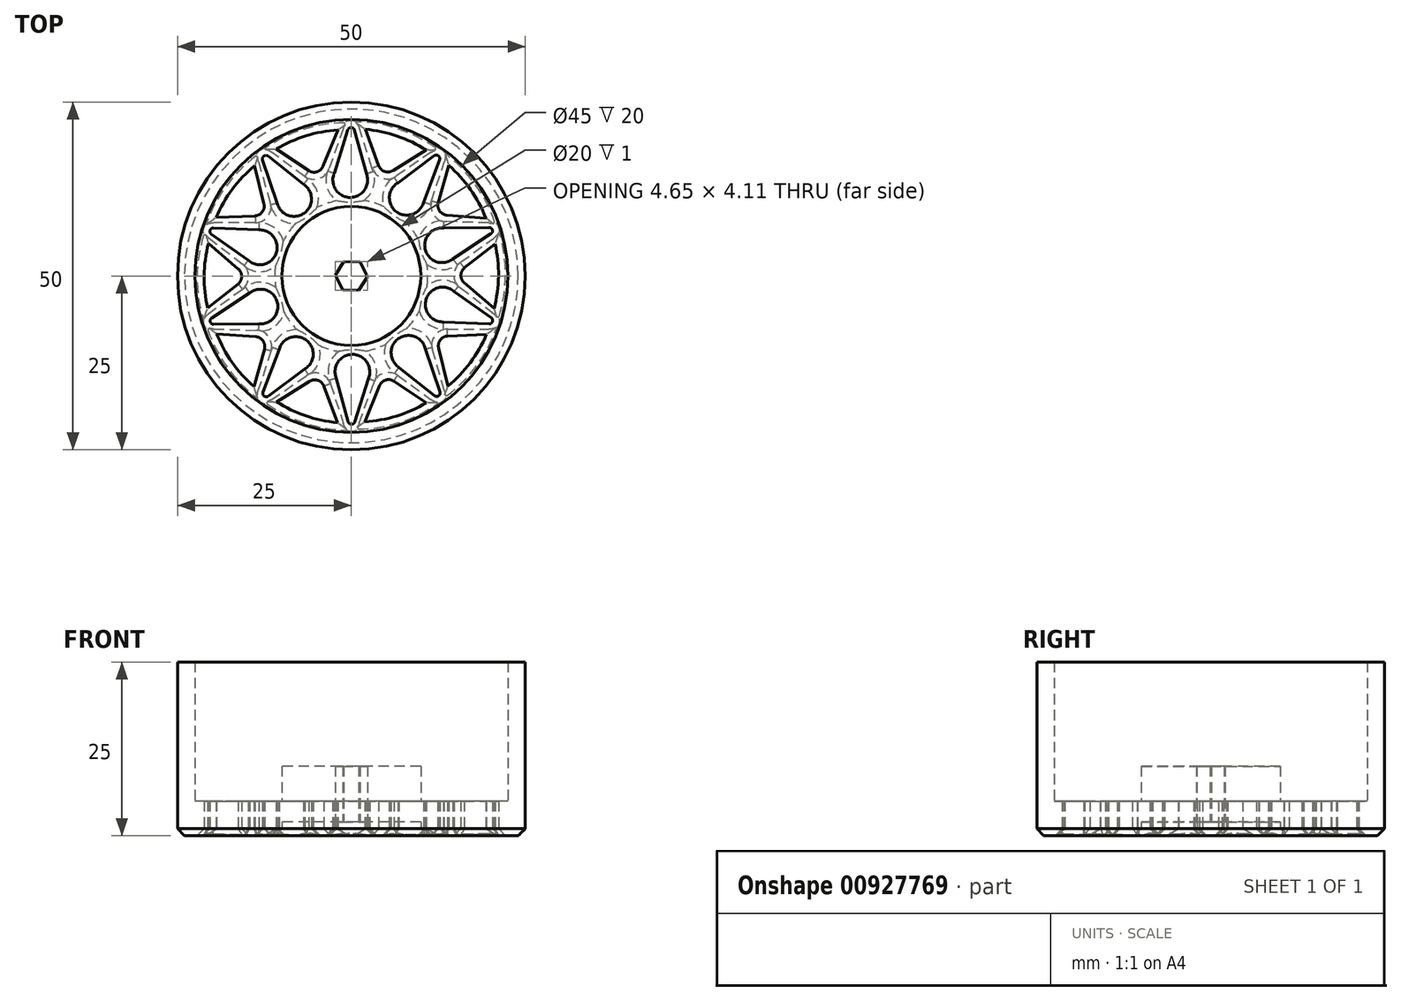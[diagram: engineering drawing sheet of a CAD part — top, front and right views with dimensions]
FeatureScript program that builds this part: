
annotation { "Feature Type Name" : "Feature", "Feature Type Description" : "" }
export const myFeature = defineFeature(function(context is Context, id is Id, definition is map)
    precondition{}
    {
        {
            var Q0;
            Q0=qCreatedBy(makeId("Top.planeOp"),FACE);
            var sketch = newSketch(context, id + "F0", { "sketchPlane" : qUnion([Q0])});
            skCircle(sketch, "E0", {"center": v(0, 0) * mm, "radius": 25 * mm});
            skCircle(sketch, "E1", {"center": v(0, 0) * mm, "radius": 22.5 * mm});
            skCircle(sketch, "E2", {"center": v(0, 0) * mm, "radius": 10 * mm});
            skLineSegment(sketch, "E3", {"start": v(0, 10) * mm, "end": v(0, 22.5) * mm, "construction": true});
            skPoint(sketch, "E4", {"position": v(0, 16.25) * mm});
            skCircle(sketch, "E5", {"center": v(-0.16, 13.78) * mm, "radius": 2.5 * mm});
            skPoint(sketch, "E6", {"position": v(0, 22.61) * mm});
            skLineSegment(sketch, "E7", {"start": v(-2.63, 14.21) * mm, "end": v(2.3, 14.21) * mm, "construction": true});
            skLineSegment(sketch, "E8", {"start": v(-0.5, 20.99) * mm, "end": v(-2.63, 14.21) * mm});
            skLineSegment(sketch, "E9", {"start": v(0.45, 20.97) * mm, "end": v(2.3, 14.21) * mm});
            skArc(sketch, "E10.filletArc", {"start": v(0.45, 20.97) * mm, "mid": v(-0.02, 21.34) * mm, "end": v(-0.5, 20.99) * mm});
            skCircle(sketch, "E11.1.0", {"center": v(-8.23, 11.06) * mm, "radius": 2.5 * mm});
            skLineSegment(sketch, "E11.1.1", {"start": v(-11.96, 17.23) * mm, "end": v(-6.49, 12.85) * mm});
            skLineSegment(sketch, "E11.1.2", {"start": v(-12.75, 16.68) * mm, "end": v(-10.48, 9.95) * mm});
            skArc(sketch, "E11.1.3", {"start": v(-11.96, 17.23) * mm, "mid": v(-12.56, 17.25) * mm, "end": v(-12.75, 16.68) * mm});
            skCircle(sketch, "E11.2.0", {"center": v(-13.15, 4.11) * mm, "radius": 2.5 * mm});
            skLineSegment(sketch, "E11.2.1", {"start": v(-19.8, 6.9) * mm, "end": v(-12.8, 6.59) * mm});
            skLineSegment(sketch, "E11.2.2", {"start": v(-20.12, 6) * mm, "end": v(-14.33, 1.9) * mm});
            skArc(sketch, "E11.2.3", {"start": v(-19.8, 6.9) * mm, "mid": v(-20.3, 6.57) * mm, "end": v(-20.12, 6) * mm});
            skCircle(sketch, "E11.3.0", {"center": v(-13.06, -4.4) * mm, "radius": 2.5 * mm});
            skLineSegment(sketch, "E11.3.1", {"start": v(-20.08, -6.05) * mm, "end": v(-14.23, -2.2) * mm});
            skLineSegment(sketch, "E11.3.2", {"start": v(-19.8, -6.97) * mm, "end": v(-12.7, -6.89) * mm});
            skArc(sketch, "E11.3.3", {"start": v(-20.08, -6.05) * mm, "mid": v(-20.29, -6.61) * mm, "end": v(-19.8, -6.97) * mm});
            skCircle(sketch, "E11.4.0", {"center": v(-7.97, -11.24) * mm, "radius": 2.5 * mm});
            skLineSegment(sketch, "E11.4.1", {"start": v(-12.7, -16.7) * mm, "end": v(-10.22, -10.14) * mm});
            skLineSegment(sketch, "E11.4.2", {"start": v(-11.92, -17.28) * mm, "end": v(-6.23, -13.04) * mm});
            skArc(sketch, "E11.4.3", {"start": v(-12.7, -16.7) * mm, "mid": v(-12.52, -17.28) * mm, "end": v(-11.92, -17.28) * mm});
            skCircle(sketch, "E11.5.0", {"center": v(0.16, -13.78) * mm, "radius": 2.5 * mm});
            skLineSegment(sketch, "E11.5.1", {"start": v(-0.45, -20.97) * mm, "end": v(-2.3, -14.21) * mm});
            skLineSegment(sketch, "E11.5.2", {"start": v(0.5, -20.99) * mm, "end": v(2.63, -14.21) * mm});
            skArc(sketch, "E11.5.3", {"start": v(-0.45, -20.97) * mm, "mid": v(0.02, -21.34) * mm, "end": v(0.5, -20.99) * mm});
            skCircle(sketch, "E11.6.0", {"center": v(8.23, -11.06) * mm, "radius": 2.5 * mm});
            skLineSegment(sketch, "E11.6.1", {"start": v(11.96, -17.23) * mm, "end": v(6.49, -12.85) * mm});
            skLineSegment(sketch, "E11.6.2", {"start": v(12.75, -16.68) * mm, "end": v(10.48, -9.95) * mm});
            skArc(sketch, "E11.6.3", {"start": v(11.96, -17.23) * mm, "mid": v(12.56, -17.25) * mm, "end": v(12.75, -16.68) * mm});
            skCircle(sketch, "E11.7.0", {"center": v(13.15, -4.11) * mm, "radius": 2.5 * mm});
            skLineSegment(sketch, "E11.7.1", {"start": v(19.8, -6.9) * mm, "end": v(12.8, -6.59) * mm});
            skLineSegment(sketch, "E11.7.2", {"start": v(20.12, -6) * mm, "end": v(14.33, -1.9) * mm});
            skArc(sketch, "E11.7.3", {"start": v(19.8, -6.9) * mm, "mid": v(20.3, -6.57) * mm, "end": v(20.12, -6) * mm});
            skCircle(sketch, "E11.8.0", {"center": v(13.06, 4.4) * mm, "radius": 2.5 * mm});
            skLineSegment(sketch, "E11.8.1", {"start": v(20.08, 6.05) * mm, "end": v(14.23, 2.2) * mm});
            skLineSegment(sketch, "E11.8.2", {"start": v(19.8, 6.97) * mm, "end": v(12.7, 6.89) * mm});
            skArc(sketch, "E11.8.3", {"start": v(20.08, 6.05) * mm, "mid": v(20.29, 6.61) * mm, "end": v(19.8, 6.97) * mm});
            skCircle(sketch, "E11.9.0", {"center": v(7.97, 11.24) * mm, "radius": 2.5 * mm});
            skLineSegment(sketch, "E11.9.1", {"start": v(12.7, 16.7) * mm, "end": v(10.22, 10.14) * mm});
            skLineSegment(sketch, "E11.9.2", {"start": v(11.92, 17.28) * mm, "end": v(6.23, 13.04) * mm});
            skArc(sketch, "E11.9.3", {"start": v(12.7, 16.7) * mm, "mid": v(12.52, 17.28) * mm, "end": v(11.92, 17.28) * mm});
            skLineSegment(sketch, "E12", {"start": v(-10.78, 18.23) * mm, "end": v(-6.12, 15.12) * mm});
            skPoint(sketch, "E12.endSnap0", {"position": v(-9.22, 15.04) * mm});
            skLineSegment(sketch, "E13", {"start": v(-1.93, 20.97) * mm, "end": v(-4.06, 15.78) * mm});
            skArc(sketch, "E14", {"start": v(-6.12, 15.12) * mm, "mid": v(-4.94, 14.97) * mm, "end": v(-4.06, 15.78) * mm});
            skArc(sketch, "E15", {"start": v(-1.93, 20.97) * mm, "mid": v(-6.52, 20.14) * mm, "end": v(-10.78, 18.23) * mm});
            skLineSegment(sketch, "E16.1.0", {"start": v(-19.44, 8.41) * mm, "end": v(-13.84, 8.64) * mm});
            skArc(sketch, "E16.1.1", {"start": v(-13.84, 8.64) * mm, "mid": v(-12.8, 9.21) * mm, "end": v(-12.56, 10.38) * mm});
            skLineSegment(sketch, "E16.1.2", {"start": v(-13.9, 15.83) * mm, "end": v(-12.56, 10.38) * mm});
            skArc(sketch, "E16.1.3", {"start": v(-13.9, 15.83) * mm, "mid": v(-17.11, 12.46) * mm, "end": v(-19.44, 8.41) * mm});
            skLineSegment(sketch, "E16.2.0", {"start": v(-20.67, -4.62) * mm, "end": v(-16.27, -1.15) * mm});
            skArc(sketch, "E16.2.1", {"start": v(-16.27, -1.15) * mm, "mid": v(-15.76, -0.07) * mm, "end": v(-16.26, 1.01) * mm});
            skLineSegment(sketch, "E16.2.2", {"start": v(-20.54, 4.65) * mm, "end": v(-16.26, 1.01) * mm});
            skArc(sketch, "E16.2.3", {"start": v(-20.54, 4.65) * mm, "mid": v(-21.17, 0.02) * mm, "end": v(-20.67, -4.62) * mm});
            skLineSegment(sketch, "E16.3.0", {"start": v(-14, -15.89) * mm, "end": v(-12.5, -10.5) * mm});
            skArc(sketch, "E16.3.1", {"start": v(-12.5, -10.5) * mm, "mid": v(-12.71, -9.32) * mm, "end": v(-13.75, -8.74) * mm});
            skLineSegment(sketch, "E16.3.2", {"start": v(-19.35, -8.32) * mm, "end": v(-13.75, -8.74) * mm});
            skArc(sketch, "E16.3.3", {"start": v(-19.35, -8.32) * mm, "mid": v(-17.14, -12.42) * mm, "end": v(-14, -15.89) * mm});
            skLineSegment(sketch, "E16.4.0", {"start": v(-2, -21.09) * mm, "end": v(-3.94, -15.83) * mm});
            skArc(sketch, "E16.4.1", {"start": v(-3.94, -15.83) * mm, "mid": v(-4.8, -15.01) * mm, "end": v(-5.99, -15.15) * mm});
            skLineSegment(sketch, "E16.4.2", {"start": v(-10.77, -18.1) * mm, "end": v(-5.99, -15.15) * mm});
            skArc(sketch, "E16.4.3", {"start": v(-10.77, -18.1) * mm, "mid": v(-6.56, -20.12) * mm, "end": v(-2, -21.09) * mm});
            skLineSegment(sketch, "E16.5.0", {"start": v(10.78, -18.23) * mm, "end": v(6.12, -15.12) * mm});
            skArc(sketch, "E16.5.1", {"start": v(6.12, -15.12) * mm, "mid": v(4.94, -14.97) * mm, "end": v(4.06, -15.78) * mm});
            skLineSegment(sketch, "E16.5.2", {"start": v(1.93, -20.97) * mm, "end": v(4.06, -15.78) * mm});
            skArc(sketch, "E16.5.3", {"start": v(1.93, -20.97) * mm, "mid": v(6.52, -20.14) * mm, "end": v(10.78, -18.23) * mm});
            skLineSegment(sketch, "E16.6.0", {"start": v(19.44, -8.41) * mm, "end": v(13.84, -8.64) * mm});
            skArc(sketch, "E16.6.1", {"start": v(13.84, -8.64) * mm, "mid": v(12.8, -9.21) * mm, "end": v(12.56, -10.38) * mm});
            skLineSegment(sketch, "E16.6.2", {"start": v(13.9, -15.83) * mm, "end": v(12.56, -10.38) * mm});
            skArc(sketch, "E16.6.3", {"start": v(13.9, -15.83) * mm, "mid": v(17.11, -12.46) * mm, "end": v(19.44, -8.41) * mm});
            skLineSegment(sketch, "E16.7.0", {"start": v(20.67, 4.62) * mm, "end": v(16.27, 1.15) * mm});
            skArc(sketch, "E16.7.1", {"start": v(16.27, 1.15) * mm, "mid": v(15.76, 0.07) * mm, "end": v(16.26, -1.01) * mm});
            skLineSegment(sketch, "E16.7.2", {"start": v(20.54, -4.65) * mm, "end": v(16.26, -1.01) * mm});
            skArc(sketch, "E16.7.3", {"start": v(20.54, -4.65) * mm, "mid": v(21.17, -0.02) * mm, "end": v(20.67, 4.62) * mm});
            skLineSegment(sketch, "E16.8.0", {"start": v(14, 15.89) * mm, "end": v(12.5, 10.5) * mm});
            skArc(sketch, "E16.8.1", {"start": v(12.5, 10.5) * mm, "mid": v(12.71, 9.32) * mm, "end": v(13.75, 8.74) * mm});
            skLineSegment(sketch, "E16.8.2", {"start": v(19.35, 8.32) * mm, "end": v(13.75, 8.74) * mm});
            skArc(sketch, "E16.8.3", {"start": v(19.35, 8.32) * mm, "mid": v(17.14, 12.42) * mm, "end": v(14, 15.89) * mm});
            skLineSegment(sketch, "E16.9.0", {"start": v(2, 21.09) * mm, "end": v(3.94, 15.83) * mm});
            skArc(sketch, "E16.9.1", {"start": v(3.94, 15.83) * mm, "mid": v(4.8, 15.01) * mm, "end": v(5.99, 15.15) * mm});
            skLineSegment(sketch, "E16.9.2", {"start": v(10.77, 18.1) * mm, "end": v(5.99, 15.15) * mm});
            skArc(sketch, "E16.9.3", {"start": v(10.77, 18.1) * mm, "mid": v(6.56, 20.12) * mm, "end": v(2, 21.09) * mm});
            skSolve(sketch);
        }
        {
            var Q0;
            Q0=makeQuery(id+"F0.imprint","IMPRINT",FACE,{"disambiguationData":[TD([[makeQuery(id+"F0.imprint","IMPRINT",EDGE,{"derivedFrom":sQuery(id+"F0.wireOp",EDGE,"E0")}),1.0]])]});
            extrude(context, id + "F1", {"entities" : qUnion([Q0]), "depth" : 25 * mm, "offsetDistance" : 25 * mm});
        }
        {
            var Q0;
            Q0=makeQuery(id+"F0.imprint","IMPRINT",FACE,{"disambiguationData":[TD([[makeQuery(id+"F0.imprint","IMPRINT",EDGE,{"derivedFrom":sQuery(id+"F0.wireOp",EDGE,"E1")}),1.0]])]});
            extrude(context, id + "F2", {"entities" : qUnion([Q0]), "operationType" : NewBodyOperationType.ADD, "depth" : 5 * mm, "offsetDistance" : 25 * mm});
        }
        {
            var Q0;
            {var subQ0=sQuery(id+"F0.wireOp",EDGE,"E2");var subQ1=makeQuery(id+"F0.imprint","INTERSECT",VERTEX,{"derivedFrom":[subQ0,sQuery(id+"F0.wireOp",EDGE,"FMw9U3Ag-M4uU-eOUw-AIyu-Y3kzjyrUIhWa.right")]});Q0=makeQuery(id+"F0.imprint","IMPRINT",FACE,{"disambiguationData":[TD([[makeQuery(id+"F0.imprint","IMPRINT",EDGE,{"disambiguationData":[TD([[subQ1,1.0]])],"derivedFrom":subQ0}),1.0]])]});}
            extrude(context, id + "F3", {"entities" : qUnion([Q0]), "operationType" : NewBodyOperationType.ADD, "depth" : 10 * mm, "offsetDistance" : 25 * mm});
        }
        {
            var Q0;
            Q0=makeQuery(id+"F0.imprint","IMPRINT",FACE,{"disambiguationData":[TD([[makeQuery(id+"F0.imprint","IMPRINT",EDGE,{"derivedFrom":sQuery(id+"F0.wireOp",EDGE,"E2")}),1.0]])]});
            extrude(context, id + "F4", {"entities" : qUnion([Q0]), "operationType" : NewBodyOperationType.REMOVE, "depth" : 2 * mm, "offsetDistance" : 25 * mm});
        }
        {
            var Q0;
            Q0=makeQuery(id+"F0.imprint","IMPRINT",FACE,{"disambiguationData":[TD([[makeQuery(id+"F0.imprint","IMPRINT",EDGE,{"derivedFrom":sQuery(id+"F0.wireOp",EDGE,"E2")}),1.0]])]});
            var sketch = newSketch(context, id + "F5", { "sketchPlane" : qUnion([Q0])});
            skPoint(sketch, "E17.0.midPoint", {"position": v(-1.32, 0.78) * mm});
            skCircle(sketch, "E18.cCircle", {"center": v(0, 0) * mm, "radius": 2.02 * mm, "construction": true});
            skLineSegment(sketch, "E18.0", {"start": v(-2.33, 0.08) * mm, "end": v(-1.1, 2.06) * mm});
            skLineSegment(sketch, "E18.1", {"start": v(-1.1, 2.06) * mm, "end": v(1.24, 1.97) * mm});
            skLineSegment(sketch, "E18.2", {"start": v(1.24, 1.97) * mm, "end": v(2.33, -0.08) * mm});
            skLineSegment(sketch, "E18.3", {"start": v(2.33, -0.08) * mm, "end": v(1.1, -2.06) * mm});
            skLineSegment(sketch, "E18.4", {"start": v(1.1, -2.06) * mm, "end": v(-1.24, -1.97) * mm});
            skLineSegment(sketch, "E18.5", {"start": v(-1.24, -1.97) * mm, "end": v(-2.33, 0.08) * mm});
            skPoint(sketch, "E18.0.midPoint", {"position": v(-1.7, 1.07) * mm});
            skPoint(sketch, "E19.orphan", {"position": v(-0.9, -1.52) * mm});
            skPoint(sketch, "E20.orphan", {"position": v(0.87, -1.54) * mm});
            skPoint(sketch, "E21.orphan", {"position": v(-1.77, 0.02) * mm});
            skPoint(sketch, "E17.1.start.orphan", {"position": v(-0.87, 1.54) * mm});
            skCircle(sketch, "E22.cCircle", {"center": v(0, -5.83) * mm, "radius": 1.3 * mm, "construction": true});
            skLineSegment(sketch, "E22.0", {"start": v(0.95, -7.14) * mm, "end": v(-0.95, -7.14) * mm});
            skLineSegment(sketch, "E22.1", {"start": v(-0.95, -7.14) * mm, "end": v(-1.54, -5.33) * mm});
            skLineSegment(sketch, "E22.2", {"start": v(-1.54, -5.33) * mm, "end": v(0, -4.21) * mm});
            skLineSegment(sketch, "E22.3", {"start": v(0, -4.21) * mm, "end": v(1.54, -5.33) * mm});
            skLineSegment(sketch, "E22.4", {"start": v(1.54, -5.33) * mm, "end": v(0.95, -7.14) * mm});
            skPoint(sketch, "E22.0.midPoint", {"position": v(0, -7.14) * mm});
            skLineSegment(sketch, "E23.1.0", {"start": v(5.54, -0.18) * mm, "end": v(7.08, -1.3) * mm});
            skLineSegment(sketch, "E23.1.1", {"start": v(4, -1.3) * mm, "end": v(5.54, -0.18) * mm});
            skLineSegment(sketch, "E23.1.2", {"start": v(4.6, -3.11) * mm, "end": v(4, -1.3) * mm});
            skLineSegment(sketch, "E23.1.3", {"start": v(6.5, -3.11) * mm, "end": v(4.6, -3.11) * mm});
            skLineSegment(sketch, "E23.1.4", {"start": v(7.08, -1.3) * mm, "end": v(6.5, -3.11) * mm});
            skLineSegment(sketch, "E23.2.0", {"start": v(1.89, 5.22) * mm, "end": v(3.43, 6.33) * mm});
            skLineSegment(sketch, "E23.2.1", {"start": v(2.47, 3.4) * mm, "end": v(1.89, 5.22) * mm});
            skLineSegment(sketch, "E23.2.2", {"start": v(4.38, 3.4) * mm, "end": v(2.47, 3.4) * mm});
            skLineSegment(sketch, "E23.2.3", {"start": v(4.97, 5.22) * mm, "end": v(4.38, 3.4) * mm});
            skLineSegment(sketch, "E23.2.4", {"start": v(3.43, 6.33) * mm, "end": v(4.97, 5.22) * mm});
            skLineSegment(sketch, "E23.3.0", {"start": v(-4.38, 3.4) * mm, "end": v(-4.97, 5.22) * mm});
            skLineSegment(sketch, "E23.3.1", {"start": v(-2.47, 3.4) * mm, "end": v(-4.38, 3.4) * mm});
            skLineSegment(sketch, "E23.3.2", {"start": v(-1.89, 5.22) * mm, "end": v(-2.47, 3.4) * mm});
            skLineSegment(sketch, "E23.3.3", {"start": v(-3.43, 6.33) * mm, "end": v(-1.89, 5.22) * mm});
            skLineSegment(sketch, "E23.3.4", {"start": v(-4.97, 5.22) * mm, "end": v(-3.43, 6.33) * mm});
            skLineSegment(sketch, "E23.4.0", {"start": v(-4.6, -3.11) * mm, "end": v(-6.5, -3.11) * mm});
            skLineSegment(sketch, "E23.4.1", {"start": v(-4, -1.3) * mm, "end": v(-4.6, -3.11) * mm});
            skLineSegment(sketch, "E23.4.2", {"start": v(-5.54, -0.18) * mm, "end": v(-4, -1.3) * mm});
            skLineSegment(sketch, "E23.4.3", {"start": v(-7.08, -1.3) * mm, "end": v(-5.54, -0.18) * mm});
            skLineSegment(sketch, "E23.4.4", {"start": v(-6.5, -3.11) * mm, "end": v(-7.08, -1.3) * mm});
            skSolve(sketch);
        }
        {
            var Q0;
            Q0=makeQuery(id+"F5.imprint","IMPRINT",FACE,{"disambiguationData":[TD([[makeQuery(id+"F5.imprint","IMPRINT",EDGE,{"derivedFrom":sQuery(id+"F5.wireOp",EDGE,"E18.0")}),-1.0]])]});
            extrude(context, id + "F6", {"entities" : qUnion([Q0]), "operationType" : NewBodyOperationType.REMOVE, "depth" : 25 * mm, "offsetDistance" : 25 * mm});
        }
        {
            var Q0;
            {var subQ0=sQuery(id+"F0.wireOp",EDGE,"E2");var subQ1=sQuery(id+"F0.wireOp",EDGE,"E1");Q0=makeQuery(id+"F3.boolean.opBoolean","MERGE",FACE,{"derivedFrom":[makeQuery(id+"F2.boolean.opBoolean","MERGE",FACE,{"derivedFrom":[makeQuery(id+"F1.opExtrude","CAP_FACE",FACE,{"disambiguationData":[OSD([sQuery(id+"F0.wireOp",EDGE,"E0"),subQ1])],"isStart":true}),makeQuery(id+"F2.opExtrude","CAP_FACE",FACE,{"disambiguationData":[OSD([subQ1,subQ0,sQuery(id+"F0.wireOp",EDGE,"E5"),sQuery(id+"F0.wireOp",EDGE,"E8"),sQuery(id+"F0.wireOp",EDGE,"E9"),sQuery(id+"F0.wireOp",EDGE,"E10.filletArc"),sQuery(id+"F0.wireOp",EDGE,"E11.1.0"),sQuery(id+"F0.wireOp",EDGE,"E11.1.1"),sQuery(id+"F0.wireOp",EDGE,"E11.1.2"),sQuery(id+"F0.wireOp",EDGE,"E11.1.3"),sQuery(id+"F0.wireOp",EDGE,"E11.2.0"),sQuery(id+"F0.wireOp",EDGE,"E11.2.1"),sQuery(id+"F0.wireOp",EDGE,"E11.2.2"),sQuery(id+"F0.wireOp",EDGE,"E11.2.3"),sQuery(id+"F0.wireOp",EDGE,"E11.3.0"),sQuery(id+"F0.wireOp",EDGE,"E11.3.1"),sQuery(id+"F0.wireOp",EDGE,"E11.3.2"),sQuery(id+"F0.wireOp",EDGE,"E11.3.3"),sQuery(id+"F0.wireOp",EDGE,"E11.4.0"),sQuery(id+"F0.wireOp",EDGE,"E11.4.1"),sQuery(id+"F0.wireOp",EDGE,"E11.4.2"),sQuery(id+"F0.wireOp",EDGE,"E11.4.3"),sQuery(id+"F0.wireOp",EDGE,"E11.5.0"),sQuery(id+"F0.wireOp",EDGE,"E11.5.1"),sQuery(id+"F0.wireOp",EDGE,"E11.5.2"),sQuery(id+"F0.wireOp",EDGE,"E11.5.3"),sQuery(id+"F0.wireOp",EDGE,"E11.6.0"),sQuery(id+"F0.wireOp",EDGE,"E11.6.1"),sQuery(id+"F0.wireOp",EDGE,"E11.6.2"),sQuery(id+"F0.wireOp",EDGE,"E11.6.3"),sQuery(id+"F0.wireOp",EDGE,"E11.7.0"),sQuery(id+"F0.wireOp",EDGE,"E11.7.1"),sQuery(id+"F0.wireOp",EDGE,"E11.7.2"),sQuery(id+"F0.wireOp",EDGE,"E11.7.3"),sQuery(id+"F0.wireOp",EDGE,"E11.8.0"),sQuery(id+"F0.wireOp",EDGE,"E11.8.1"),sQuery(id+"F0.wireOp",EDGE,"E11.8.2"),sQuery(id+"F0.wireOp",EDGE,"E11.8.3"),sQuery(id+"F0.wireOp",EDGE,"E11.9.0"),sQuery(id+"F0.wireOp",EDGE,"E11.9.1"),sQuery(id+"F0.wireOp",EDGE,"E11.9.2"),sQuery(id+"F0.wireOp",EDGE,"E11.9.3"),sQuery(id+"F0.wireOp",EDGE,"E12"),sQuery(id+"F0.wireOp",EDGE,"E13"),sQuery(id+"F0.wireOp",EDGE,"E14"),sQuery(id+"F0.wireOp",EDGE,"E15"),sQuery(id+"F0.wireOp",EDGE,"E16.1.0"),sQuery(id+"F0.wireOp",EDGE,"E16.1.1"),sQuery(id+"F0.wireOp",EDGE,"E16.1.2"),sQuery(id+"F0.wireOp",EDGE,"E16.1.3"),sQuery(id+"F0.wireOp",EDGE,"E16.2.0"),sQuery(id+"F0.wireOp",EDGE,"E16.2.1"),sQuery(id+"F0.wireOp",EDGE,"E16.2.2"),sQuery(id+"F0.wireOp",EDGE,"E16.2.3"),sQuery(id+"F0.wireOp",EDGE,"E16.3.0"),sQuery(id+"F0.wireOp",EDGE,"E16.3.1"),sQuery(id+"F0.wireOp",EDGE,"E16.3.2"),sQuery(id+"F0.wireOp",EDGE,"E16.3.3"),sQuery(id+"F0.wireOp",EDGE,"E16.4.0"),sQuery(id+"F0.wireOp",EDGE,"E16.4.1"),sQuery(id+"F0.wireOp",EDGE,"E16.4.2"),sQuery(id+"F0.wireOp",EDGE,"E16.4.3"),sQuery(id+"F0.wireOp",EDGE,"E16.5.0"),sQuery(id+"F0.wireOp",EDGE,"E16.5.1"),sQuery(id+"F0.wireOp",EDGE,"E16.5.2"),sQuery(id+"F0.wireOp",EDGE,"E16.5.3"),sQuery(id+"F0.wireOp",EDGE,"E16.6.0"),sQuery(id+"F0.wireOp",EDGE,"E16.6.1"),sQuery(id+"F0.wireOp",EDGE,"E16.6.2"),sQuery(id+"F0.wireOp",EDGE,"E16.6.3"),sQuery(id+"F0.wireOp",EDGE,"E16.7.0"),sQuery(id+"F0.wireOp",EDGE,"E16.7.1"),sQuery(id+"F0.wireOp",EDGE,"E16.7.2"),sQuery(id+"F0.wireOp",EDGE,"E16.7.3"),sQuery(id+"F0.wireOp",EDGE,"E16.8.0"),sQuery(id+"F0.wireOp",EDGE,"E16.8.1"),sQuery(id+"F0.wireOp",EDGE,"E16.8.2"),sQuery(id+"F0.wireOp",EDGE,"E16.8.3"),sQuery(id+"F0.wireOp",EDGE,"E16.9.0"),sQuery(id+"F0.wireOp",EDGE,"E16.9.1"),sQuery(id+"F0.wireOp",EDGE,"E16.9.2"),sQuery(id+"F0.wireOp",EDGE,"E16.9.3")])],"isStart":true})]}),makeQuery(id+"F3.opExtrude","CAP_FACE",FACE,{"disambiguationData":[OSD([subQ0])],"isStart":true})]});}
            chamfer(context, id + "F7", {"entities" : qUnion([Q0]), "width" : 1 * mm, "tangentPropagation" : true});
        }
    });
